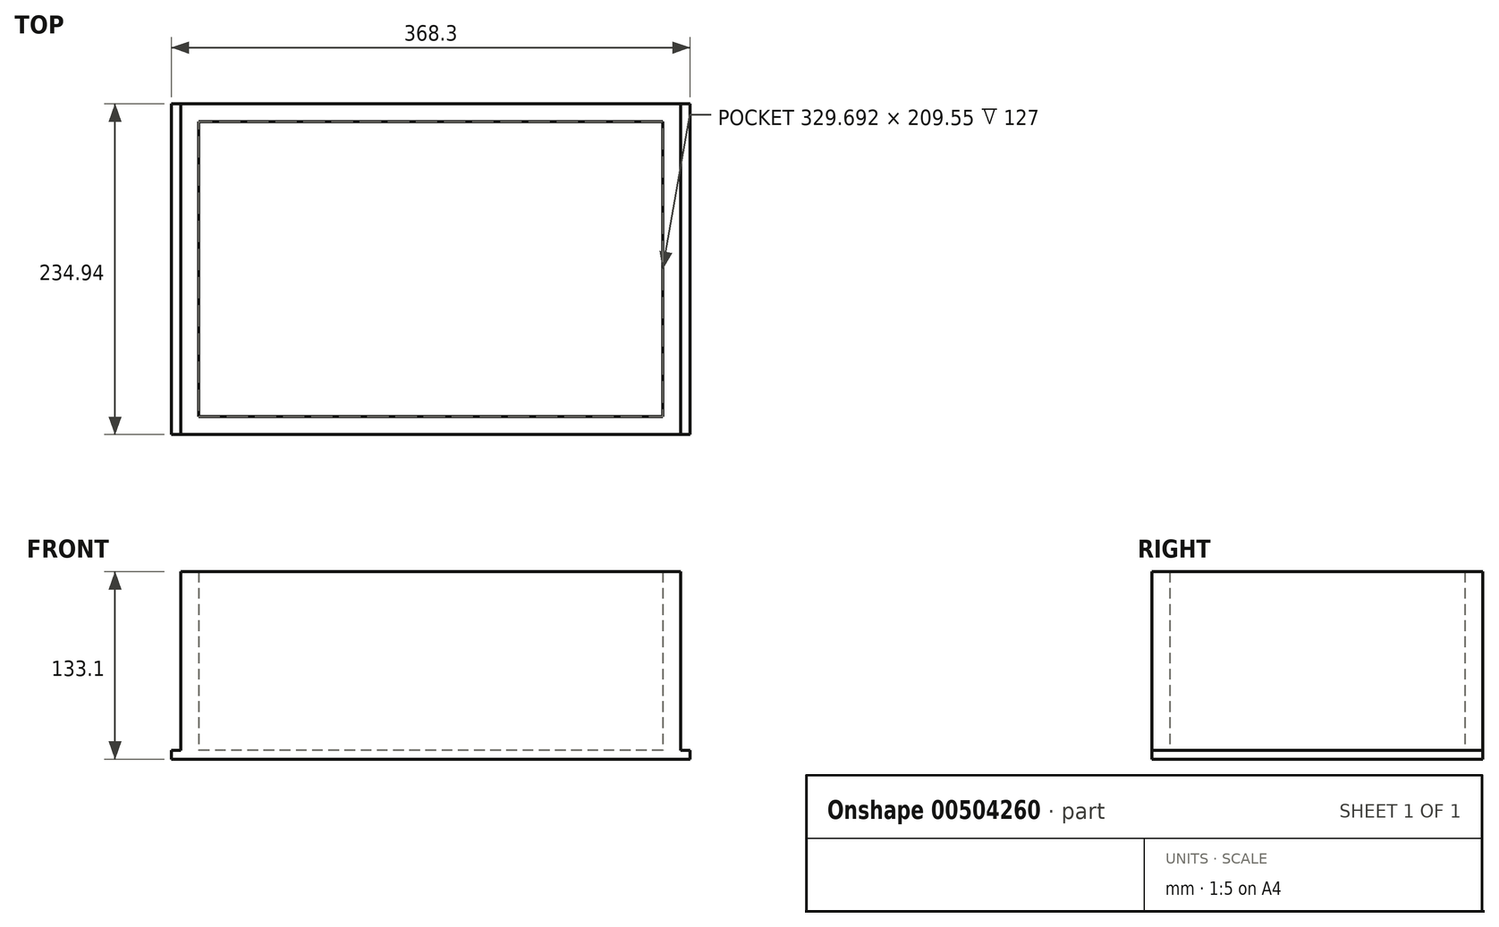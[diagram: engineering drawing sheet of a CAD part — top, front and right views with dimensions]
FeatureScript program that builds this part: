
annotation { "Feature Type Name" : "Feature", "Feature Type Description" : "" }
export const myFeature = defineFeature(function(context is Context, id is Id, definition is map)
    precondition{}
    {
        {
            var Q0;
            Q0=qCreatedBy(makeId("Top.planeOp"),FACE);
            var sketch = newSketch(context, id + "F0", { "sketchPlane" : qUnion([Q0])});
            skLineSegment(sketch, "E0.bottom", {"start": v(184.15, -117.47) * mm, "end": v(-184.15, -117.48) * mm});
            skLineSegment(sketch, "E0.top", {"start": v(184.15, 117.48) * mm, "end": v(-184.15, 117.47) * mm});
            skLineSegment(sketch, "E0.left", {"start": v(184.15, -117.47) * mm, "end": v(184.15, 117.48) * mm});
            skLineSegment(sketch, "E0.right", {"start": v(-184.15, -117.48) * mm, "end": v(-184.15, 117.48) * mm});
            skPoint(sketch, "E0.middle", {"position": v(0, 0) * mm});
            skSolve(sketch);
        }
        {
            var Q0;
            Q0=makeQuery(id+"F0.imprint","IMPRINT",FACE,{"disambiguationData":[TD([[makeQuery(id+"F0.imprint","IMPRINT",EDGE,{"derivedFrom":sQuery(id+"F0.wireOp",EDGE,"E0.bottom")}),-1.0]])]});
            extrude(context, id + "F1", {"entities" : qUnion([Q0]), "depth" : 6.1 * mm});
        }
        {
            var Q0;
            Q0=makeQuery(id+"F1.opExtrude","CAP_FACE",FACE,{"disambiguationData":[OSD([sQuery(id+"F0.wireOp",EDGE,"E0.bottom"),sQuery(id+"F0.wireOp",EDGE,"E0.top"),sQuery(id+"F0.wireOp",EDGE,"E0.left"),sQuery(id+"F0.wireOp",EDGE,"E0.right")])],"isStart":false});
            var sketch = newSketch(context, id + "F2", { "sketchPlane" : qUnion([Q0])});
            skLineSegment(sketch, "E1.bottom", {"start": v(177.55, 117.48) * mm, "end": v(-177.55, 117.48) * mm});
            skLineSegment(sketch, "E1.top", {"start": v(177.55, 104.78) * mm, "end": v(-177.55, 104.77) * mm});
            skLineSegment(sketch, "E1.left", {"start": v(177.55, 117.48) * mm, "end": v(177.55, 104.78) * mm});
            skLineSegment(sketch, "E1.right", {"start": v(-177.55, 117.47) * mm, "end": v(-177.55, 104.77) * mm});
            skLineSegment(sketch, "E2.bottom", {"start": v(-177.55, -117.48) * mm, "end": v(177.55, -117.48) * mm});
            skLineSegment(sketch, "E2.top", {"start": v(-177.55, -104.78) * mm, "end": v(177.55, -104.78) * mm});
            skLineSegment(sketch, "E2.left", {"start": v(-177.55, -117.48) * mm, "end": v(-177.55, -104.78) * mm});
            skLineSegment(sketch, "E2.right", {"start": v(177.55, -117.48) * mm, "end": v(177.55, -104.77) * mm});
            skLineSegment(sketch, "E3.bottom", {"start": v(177.55, -104.77) * mm, "end": v(164.85, -104.77) * mm});
            skLineSegment(sketch, "E3.top", {"start": v(177.55, 104.78) * mm, "end": v(164.85, 104.78) * mm});
            skLineSegment(sketch, "E3.left", {"start": v(177.55, -104.77) * mm, "end": v(177.55, 104.78) * mm});
            skLineSegment(sketch, "E3.right", {"start": v(164.85, -104.77) * mm, "end": v(164.85, 104.78) * mm});
            skLineSegment(sketch, "E4.bottom", {"start": v(-177.55, -104.78) * mm, "end": v(-164.85, -104.78) * mm});
            skLineSegment(sketch, "E4.top", {"start": v(-177.55, 104.77) * mm, "end": v(-164.85, 104.77) * mm});
            skLineSegment(sketch, "E4.left", {"start": v(-177.55, -104.78) * mm, "end": v(-177.55, 104.77) * mm});
            skLineSegment(sketch, "E4.right", {"start": v(-164.85, -104.78) * mm, "end": v(-164.85, 104.77) * mm});
            skSolve(sketch);
        }
        {
            var Q0;
            {var subQ2=sQuery(id+"F2.wireOp",EDGE,"E3.left");Q0=makeQuery(id+"F2.imprint","IMPRINT",FACE,{"disambiguationData":[TD([[makeQuery(id+"F2.imprint","IMPRINT",EDGE,{"derivedFrom":subQ2}),1.0]])]});}
            var Q1;
            Q1=makeQuery(id+"F2.imprint","IMPRINT",FACE,{"disambiguationData":[TD([[makeQuery(id+"F2.imprint","IMPRINT",EDGE,{"derivedFrom":sQuery(id+"F2.wireOp",EDGE,"E1.bottom")}),1.0]])]});
            var Q2;
            {var subQ0=sQuery(id+"F2.wireOp",EDGE,"E4.left");Q2=makeQuery(id+"F2.imprint","IMPRINT",FACE,{"disambiguationData":[TD([[makeQuery(id+"F2.imprint","IMPRINT",EDGE,{"derivedFrom":subQ0}),-1.0]])]});}
            var Q3;
            Q3=makeQuery(id+"F2.imprint","IMPRINT",FACE,{"disambiguationData":[TD([[makeQuery(id+"F2.imprint","IMPRINT",EDGE,{"derivedFrom":sQuery(id+"F2.wireOp",EDGE,"E2.bottom")}),-1.0]])]});
            extrude(context, id + "F3", {"entities" : qUnion([Q0, Q1, Q2, Q3]), "operationType" : NewBodyOperationType.ADD, "depth" : 127 * mm});
        }
    });
